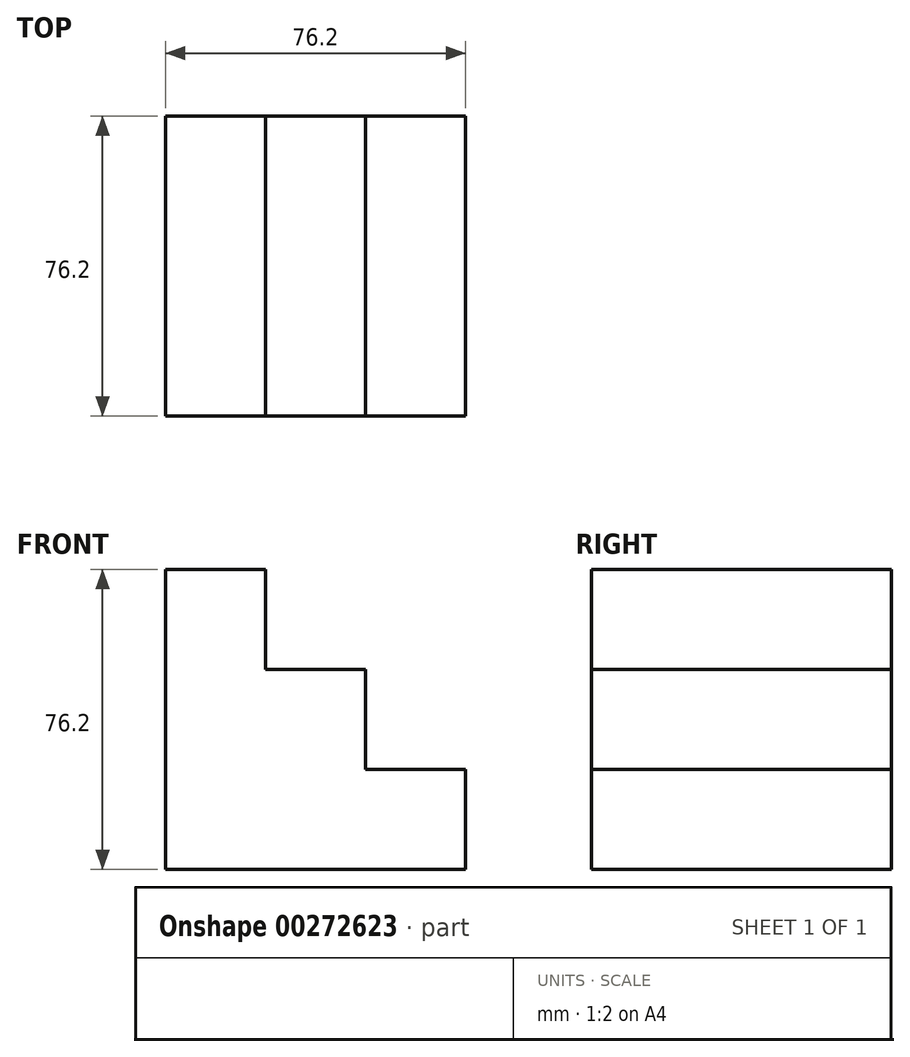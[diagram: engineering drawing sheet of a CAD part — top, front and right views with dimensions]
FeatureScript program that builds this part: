
annotation { "Feature Type Name" : "Feature", "Feature Type Description" : "" }
export const myFeature = defineFeature(function(context is Context, id is Id, definition is map)
    precondition{}
    {
        {
            var Q0;
            Q0=qCreatedBy(makeId("Front.planeOp"),FACE);
            var sketch = newSketch(context, id + "F0", { "sketchPlane" : qUnion([Q0])});
            skLineSegment(sketch, "E0", {"start": v(0, 0) * mm, "end": v(-76.2, 0) * mm});
            skLineSegment(sketch, "E1", {"start": v(-76.2, 0) * mm, "end": v(-76.2, 76.2) * mm});
            skLineSegment(sketch, "E2", {"start": v(-76.2, 76.2) * mm, "end": v(-50.8, 76.2) * mm});
            skLineSegment(sketch, "E3", {"start": v(0, 0) * mm, "end": v(0, 25.4) * mm});
            skLineSegment(sketch, "E4", {"start": v(0, 25.4) * mm, "end": v(-25.4, 25.4) * mm});
            skLineSegment(sketch, "E5", {"start": v(-25.4, 25.4) * mm, "end": v(-25.4, 50.8) * mm});
            skLineSegment(sketch, "E6", {"start": v(-25.4, 50.8) * mm, "end": v(-50.8, 50.8) * mm});
            skLineSegment(sketch, "E7", {"start": v(-50.8, 76.2) * mm, "end": v(-50.8, 50.8) * mm});
            skSolve(sketch);
        }
        {
            var Q0;
            Q0 = qSketchRegion(id + "F0", true);
            extrude(context, id + "F1", {"entities" : qUnion([Q0]), "depth" : 76.2 * mm});
        }
    });
